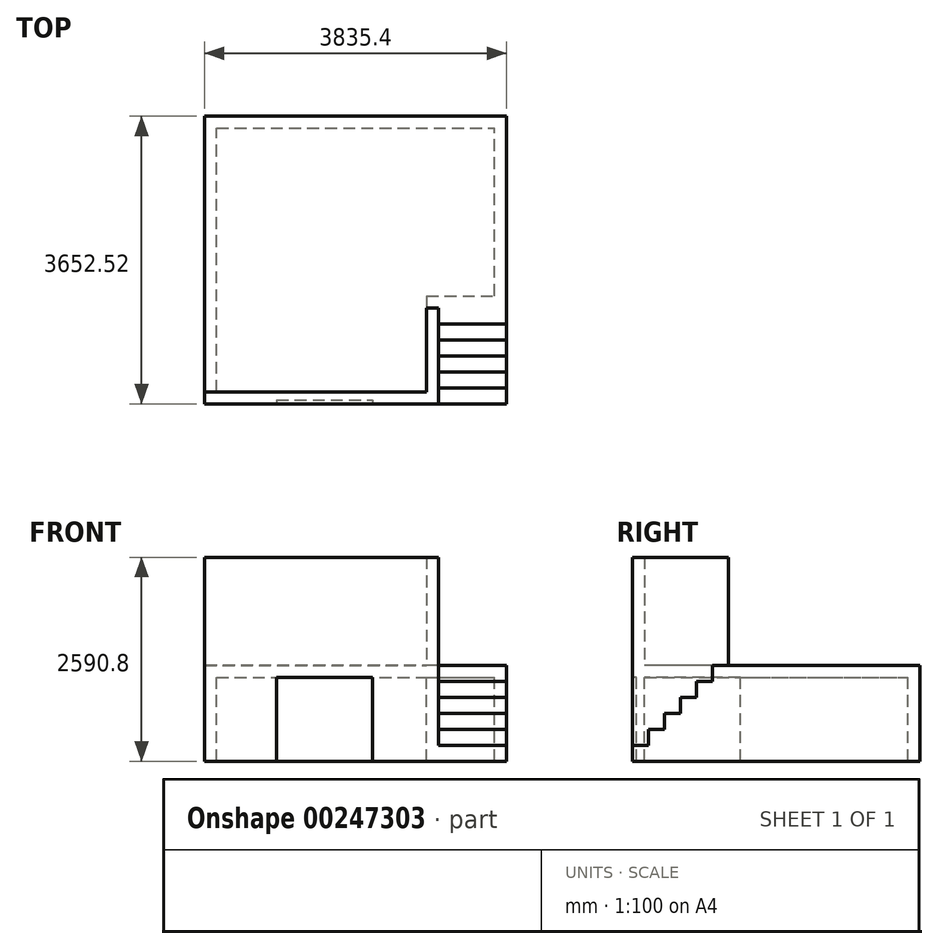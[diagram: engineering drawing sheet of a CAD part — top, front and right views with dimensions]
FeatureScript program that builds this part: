
annotation { "Feature Type Name" : "Feature", "Feature Type Description" : "" }
export const myFeature = defineFeature(function(context is Context, id is Id, definition is map)
    precondition{}
    {
        {
            var Q0;
            Q0=qCreatedBy(makeId("Top.planeOp"),FACE);
            var sketch = newSketch(context, id + "F0", { "sketchPlane" : qUnion([Q0])});
            skLineSegment(sketch, "E0.bottom", {"start": v(0, 0) * mm, "end": v(3835.4, 0) * mm});
            skLineSegment(sketch, "E0.top", {"start": v(0, 3652.52) * mm, "end": v(3835.4, 3652.52) * mm});
            skLineSegment(sketch, "E0.left", {"start": v(0, 0) * mm, "end": v(0, 3652.52) * mm});
            skLineSegment(sketch, "E0.right", {"start": v(3835.4, 0) * mm, "end": v(3835.4, 3652.52) * mm});
            skLineSegment(sketch, "E1.0", {"start": v(152.4, 152.4) * mm, "end": v(152.4, 3500.12) * mm});
            skLineSegment(sketch, "E1.1", {"start": v(152.4, 152.4) * mm, "end": v(3683, 152.4) * mm});
            skLineSegment(sketch, "E1.2", {"start": v(3683, 152.4) * mm, "end": v(3683, 3500.12) * mm});
            skLineSegment(sketch, "E1.3", {"start": v(152.4, 3500.12) * mm, "end": v(3683, 3500.12) * mm});
            skSolve(sketch);
        }
        {
            var Q0;
            Q0 = qSketchRegion(id + "F0", true);
            extrude(context, id + "F1", {"entities" : qUnion([Q0]), "oppositeDirection" : true, "depth" : 1066.8 * mm});
        }
        {
            var Q0;
            Q0=makeQuery(id+"F1.opExtrude","SWEPT_FACE",FACE,{"disambiguationData":[OSD([sQuery(id+"F0.wireOp",EDGE,"E0.bottom")])]});
            var sketch = newSketch(context, id + "F2", { "sketchPlane" : qUnion([Q0])});
            skLineSegment(sketch, "E2.bottom", {"start": v(0, 0) * mm, "end": v(3835.4, 0) * mm});
            skLineSegment(sketch, "E2.top", {"start": v(0, 152.4) * mm, "end": v(3835.4, 152.4) * mm});
            skLineSegment(sketch, "E2.left", {"start": v(0, 0) * mm, "end": v(0, 152.4) * mm});
            skLineSegment(sketch, "E2.right", {"start": v(3835.4, 0) * mm, "end": v(3835.4, 152.4) * mm});
            skSolve(sketch);
        }
        {
            var Q0;
            Q0=makeQuery(id+"F2.imprint","IMPRINT",FACE,{"disambiguationData":[TD([[makeQuery(id+"F2.imprint","IMPRINT",EDGE,{"derivedFrom":sQuery(id+"F2.wireOp",EDGE,"E2.bottom")}),1.0]])]});
            var Q1;
            Q1=makeQuery(id+"F1.opExtrude","SWEPT_FACE",FACE,{"disambiguationData":[OSD([sQuery(id+"F0.wireOp",EDGE,"E0.top")])]});
            extrude(context, id + "F3", {"entities" : qUnion([Q0]), "operationType" : NewBodyOperationType.ADD, "endBound" : BoundingType.UP_TO_SURFACE, "oppositeDirection" : true, "endBoundEntityFace" : qUnion([Q1]), "depth" : 25.4 * mm});
        }
        {
            var Q0;
            Q0=makeQuery(id+"F3.opExtrude","SWEPT_FACE",FACE,{"disambiguationData":[OSD([sQuery(id+"F2.wireOp",EDGE,"E2.top")])]});
            var sketch = newSketch(context, id + "F4", { "sketchPlane" : qUnion([Q0])});
            skLineSegment(sketch, "E3.bottom", {"start": v(3835.4, 0) * mm, "end": v(2971.8, 0) * mm});
            skLineSegment(sketch, "E3.top", {"start": v(3835.4, 1219.2) * mm, "end": v(2971.8, 1219.2) * mm});
            skLineSegment(sketch, "E3.left", {"start": v(3835.4, 0) * mm, "end": v(3835.4, 1219.2) * mm});
            skLineSegment(sketch, "E3.right", {"start": v(2971.8, 0) * mm, "end": v(2971.8, 1219.2) * mm});
            skSolve(sketch);
        }
        {
            var Q0;
            Q0=makeQuery(id+"F4.imprint","IMPRINT",FACE,{"disambiguationData":[TD([[makeQuery(id+"F4.imprint","IMPRINT",EDGE,{"derivedFrom":sQuery(id+"F4.wireOp",EDGE,"E3.bottom")}),1.0]])]});
            var Q1;
            Q1=makeQuery(id+"F1.opExtrude","CAP_FACE",FACE,{"disambiguationData":[OSD([sQuery(id+"F0.wireOp",EDGE,"E0.bottom"),sQuery(id+"F0.wireOp",EDGE,"E0.top"),sQuery(id+"F0.wireOp",EDGE,"E0.left"),sQuery(id+"F0.wireOp",EDGE,"E0.right"),sQuery(id+"F0.wireOp",EDGE,"E1.0"),sQuery(id+"F0.wireOp",EDGE,"E1.1"),sQuery(id+"F0.wireOp",EDGE,"E1.2"),sQuery(id+"F0.wireOp",EDGE,"E1.3")])],"isStart":false});
            extrude(context, id + "F5", {"entities" : qUnion([Q0]), "operationType" : NewBodyOperationType.REMOVE, "endBound" : BoundingType.UP_TO_SURFACE, "oppositeDirection" : true, "endBoundEntityFace" : qUnion([Q1]), "depth" : 25.4 * mm});
        }
        {
            var Q0;
            Q0=makeQuery(id+"F3.opExtrude","SWEPT_FACE",FACE,{"disambiguationData":[OSD([sQuery(id+"F2.wireOp",EDGE,"E2.bottom")])]});
            var sketch = newSketch(context, id + "F6", { "sketchPlane" : qUnion([Q0])});
            skLineSegment(sketch, "E4.0", {"start": v(2819.4, -1371.6) * mm, "end": v(2819.4, -152.4) * mm});
            skLineSegment(sketch, "E4.1", {"start": v(2819.4, -1371.6) * mm, "end": v(3683, -1371.6) * mm});
            skLineSegment(sketch, "E5", {"start": v(2819.4, -152.4) * mm, "end": v(2971.8, -152.4) * mm});
            skLineSegment(sketch, "E6", {"start": v(2971.8, -152.4) * mm, "end": v(2971.8, -1219.2) * mm});
            skLineSegment(sketch, "E7", {"start": v(2971.8, -1219.2) * mm, "end": v(3683, -1219.2) * mm});
            skLineSegment(sketch, "E8", {"start": v(3683, -1219.2) * mm, "end": v(3683, -1371.6) * mm});
            skSolve(sketch);
        }
        {
            var Q0;
            Q0=makeQuery(id+"F6.imprint","IMPRINT",FACE,{"disambiguationData":[TD([[makeQuery(id+"F6.imprint","IMPRINT",EDGE,{"derivedFrom":sQuery(id+"F6.wireOp",EDGE,"E4.0")}),-1.0]])]});
            var Q1;
            Q1=makeQuery(id+"F1.opExtrude","CAP_FACE",FACE,{"disambiguationData":[OSD([sQuery(id+"F0.wireOp",EDGE,"E0.bottom"),sQuery(id+"F0.wireOp",EDGE,"E0.top"),sQuery(id+"F0.wireOp",EDGE,"E0.left"),sQuery(id+"F0.wireOp",EDGE,"E0.right"),sQuery(id+"F0.wireOp",EDGE,"E1.0"),sQuery(id+"F0.wireOp",EDGE,"E1.1"),sQuery(id+"F0.wireOp",EDGE,"E1.2"),sQuery(id+"F0.wireOp",EDGE,"E1.3")])],"isStart":false});
            extrude(context, id + "F7", {"entities" : qUnion([Q0]), "operationType" : NewBodyOperationType.ADD, "endBound" : BoundingType.UP_TO_SURFACE, "endBoundEntityFace" : qUnion([Q1]), "depth" : 25.4 * mm});
        }
        {
            var Q0;
            Q0=makeQuery(id+"F3.boolean.opBoolean","MERGE",FACE,{"derivedFrom":[makeQuery(id+"F1.opExtrude","SWEPT_FACE",FACE,{"disambiguationData":[OSD([sQuery(id+"F0.wireOp",EDGE,"E0.bottom")])]}),makeQuery(id+"F3.opExtrude","CAP_FACE",FACE,{"disambiguationData":[OSD([sQuery(id+"F2.wireOp",EDGE,"E2.bottom"),sQuery(id+"F2.wireOp",EDGE,"E2.top"),sQuery(id+"F2.wireOp",EDGE,"E2.left"),sQuery(id+"F2.wireOp",EDGE,"E2.right")])],"isStart":true})]});
            var sketch = newSketch(context, id + "F8", { "sketchPlane" : qUnion([Q0])});
            skLineSegment(sketch, "E9.bottom", {"start": v(914.4, -1066.8) * mm, "end": v(2133.6, -1066.8) * mm});
            skLineSegment(sketch, "E9.top", {"start": v(914.4, 0) * mm, "end": v(2133.6, 0) * mm});
            skLineSegment(sketch, "E9.left", {"start": v(914.4, -1066.8) * mm, "end": v(914.4, 0) * mm});
            skLineSegment(sketch, "E9.right", {"start": v(2133.6, -1066.8) * mm, "end": v(2133.6, 0) * mm});
            skSolve(sketch);
        }
        {
            var Q0;
            Q0=makeQuery(id+"F8.imprint","IMPRINT",FACE,{"disambiguationData":[TD([[makeQuery(id+"F8.imprint","IMPRINT",EDGE,{"derivedFrom":sQuery(id+"F8.wireOp",EDGE,"E9.bottom")}),1.0]])]});
            extrude(context, id + "F9", {"entities" : qUnion([Q0]), "operationType" : NewBodyOperationType.REMOVE, "oppositeDirection" : true, "depth" : 50.8 * mm});
        }
        {
            var Q0;
            Q0=makeQuery(id+"F3.boolean.opBoolean","MERGE",FACE,{"derivedFrom":[makeQuery(id+"F1.opExtrude","SWEPT_FACE",FACE,{"disambiguationData":[OSD([sQuery(id+"F0.wireOp",EDGE,"E0.right")])]}),makeQuery(id+"F3.opExtrude","SWEPT_FACE",FACE,{"disambiguationData":[OSD([sQuery(id+"F2.wireOp",EDGE,"E2.right")])]})]});
            var sketch = newSketch(context, id + "F10", { "sketchPlane" : qUnion([Q0])});
            skLineSegment(sketch, "E10", {"start": v(1219.2, -1066.8) * mm, "end": v(0, -1066.8) * mm});
            skLineSegment(sketch, "E11", {"start": v(0, -1066.8) * mm, "end": v(0, -863.6) * mm});
            skLineSegment(sketch, "E12", {"start": v(0, -863.6) * mm, "end": v(203.2, -863.6) * mm});
            skLineSegment(sketch, "E13", {"start": v(203.2, -863.6) * mm, "end": v(203.2, -660.4) * mm});
            skLineSegment(sketch, "E14", {"start": v(203.2, -660.4) * mm, "end": v(406.4, -660.4) * mm});
            skLineSegment(sketch, "E15", {"start": v(406.4, -660.4) * mm, "end": v(406.4, -457.2) * mm});
            skLineSegment(sketch, "E16", {"start": v(406.4, -457.2) * mm, "end": v(609.6, -457.2) * mm});
            skLineSegment(sketch, "E17", {"start": v(609.6, -457.2) * mm, "end": v(609.6, -254) * mm});
            skLineSegment(sketch, "E18", {"start": v(609.6, -254) * mm, "end": v(812.8, -254) * mm});
            skLineSegment(sketch, "E19", {"start": v(812.8, -254) * mm, "end": v(812.8, -50.8) * mm});
            skLineSegment(sketch, "E20", {"start": v(1016, 152.4) * mm, "end": v(1219.2, 152.4) * mm});
            skLineSegment(sketch, "E21", {"start": v(1016, 152.4) * mm, "end": v(1016, -50.8) * mm});
            skLineSegment(sketch, "E22", {"start": v(1016, -50.8) * mm, "end": v(812.8, -50.8) * mm});
            skSolve(sketch);
        }
        {
            var Q0;
            Q0=makeQuery(id+"F10.imprint","IMPRINT",FACE,{"disambiguationData":[TD([[makeQuery(id+"F10.imprint","IMPRINT",EDGE,{"derivedFrom":sQuery(id+"F10.wireOp",EDGE,"E10")}),-1.0]])]});
            var Q1;
            Q1=makeQuery(id+"F7.boolean.opBoolean","MERGE",FACE,{"derivedFrom":[makeQuery(id+"F5.boolean.opBoolean","COPY",FACE,{"derivedFrom":makeQuery(id+"F5.opExtrude","SWEPT_FACE",FACE,{"disambiguationData":[OSD([sQuery(id+"F4.wireOp",EDGE,"E3.right")])]})}),makeQuery(id+"F7.opExtrude","SWEPT_FACE",FACE,{"disambiguationData":[OSD([sQuery(id+"F6.wireOp",EDGE,"E6")])]})]});
            extrude(context, id + "F11", {"entities" : qUnion([Q0]), "operationType" : NewBodyOperationType.ADD, "endBound" : BoundingType.UP_TO_SURFACE, "oppositeDirection" : true, "endBoundEntityFace" : qUnion([Q1]), "depth" : 25.4 * mm});
        }
        {
            var Q0;
            Q0=makeQuery(id+"F11.boolean.opBoolean","MERGE",FACE,{"derivedFrom":[makeQuery(id+"F3.opExtrude","SWEPT_FACE",FACE,{"disambiguationData":[OSD([sQuery(id+"F2.wireOp",EDGE,"E2.top")])]}),makeQuery(id+"F11.opExtrude","SWEPT_FACE",FACE,{"disambiguationData":[OSD([sQuery(id+"F10.wireOp",EDGE,"E20")])]})]});
            var sketch = newSketch(context, id + "F12", { "sketchPlane" : qUnion([Q0])});
            skLineSegment(sketch, "E23.0", {"start": v(0, 0) * mm, "end": v(2971.8, 0) * mm});
            skLineSegment(sketch, "E24.0", {"start": v(0, 152.4) * mm, "end": v(2819.4, 152.4) * mm});
            skLineSegment(sketch, "E25", {"start": v(0, 152.4) * mm, "end": v(0, 0) * mm});
            skLineSegment(sketch, "E26", {"start": v(2971.8, 152.4) * mm, "end": v(2971.8, 0) * mm});
            skLineSegment(sketch, "E27.0", {"start": v(2819.4, 1219.2) * mm, "end": v(2819.4, 152.4) * mm});
            skLineSegment(sketch, "E28.0", {"start": v(2971.8, 152.4) * mm, "end": v(2971.8, 1219.2) * mm});
            skLineSegment(sketch, "E29", {"start": v(2971.8, 1219.2) * mm, "end": v(2819.4, 1219.2) * mm});
            skPoint(sketch, "E30.orphan", {"position": v(2819.4, 1371.6) * mm});
            skSolve(sketch);
        }
        {
            var Q0;
            Q0=makeQuery(id+"F12.imprint","IMPRINT",FACE,{"disambiguationData":[TD([[makeQuery(id+"F12.imprint","IMPRINT",EDGE,{"derivedFrom":sQuery(id+"F12.wireOp",EDGE,"E23.0")}),1.0]])]});
            extrude(context, id + "F13", {"entities" : qUnion([Q0]), "operationType" : NewBodyOperationType.ADD, "depth" : 1371.6 * mm});
        }
    });
